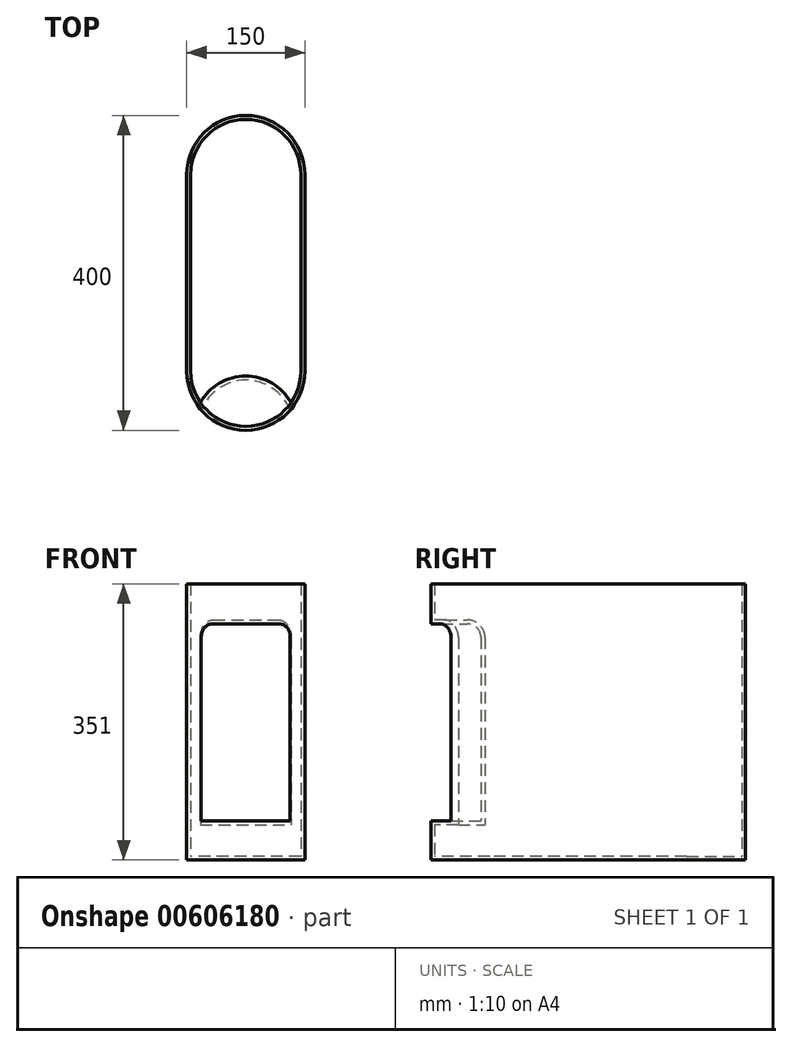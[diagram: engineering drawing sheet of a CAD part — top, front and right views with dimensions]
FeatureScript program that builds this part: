
annotation { "Feature Type Name" : "Feature", "Feature Type Description" : "" }
export const myFeature = defineFeature(function(context is Context, id is Id, definition is map)
    precondition{}
    {
        {
            var Q0;
            Q0=qCreatedBy(makeId("Top.planeOp"),FACE);
            var sketch = newSketch(context, id + "F0", { "sketchPlane" : qUnion([Q0])});
            skLineSegment(sketch, "E0", {"start": v(0, 200) * mm, "end": v(0, -200) * mm, "construction": true});
            skArc(sketch, "E1", {"start": v(75, 125) * mm, "mid": v(0, 200) * mm, "end": v(-75, 125) * mm});
            skArc(sketch, "E2", {"start": v(-75, -125) * mm, "mid": v(0, -200) * mm, "end": v(75, -125) * mm});
            skLineSegment(sketch, "E3", {"start": v(-75, 125) * mm, "end": v(-75, -125) * mm});
            skLineSegment(sketch, "E4", {"start": v(75, 125) * mm, "end": v(75, -125) * mm});
            skSolve(sketch);
        }
        {
            var Q0;
            Q0 = qSketchRegion(id + "F0", true);
            extrude(context, id + "F1", {"entities" : qUnion([Q0]), "depth" : 350 * mm, "offsetDistance" : 25 * mm});
        }
        {
            var Q0;
            Q0=qCreatedBy(makeId("Right.planeOp"),FACE);
            var sketch = newSketch(context, id + "F2", { "sketchPlane" : qUnion([Q0])});
            skLineSegment(sketch, "E5.bottom", {"start": v(-258.2, 300) * mm, "end": v(-197.2, 300) * mm});
            skLineSegment(sketch, "E5.top", {"start": v(-258.2, 50) * mm, "end": v(-197.2, 50) * mm});
            skLineSegment(sketch, "E5.left", {"start": v(-258.2, 300) * mm, "end": v(-258.2, 50) * mm});
            skLineSegment(sketch, "E5.right", {"start": v(-197.2, 300) * mm, "end": v(-197.2, 50) * mm});
            skSolve(sketch);
        }
        {
            var Q0;
            Q0=makeQuery(id+"F1.opExtrude","CAP_FACE",FACE,{"disambiguationData":[OSD([sQuery(id+"F0.wireOp",EDGE,"E1"),sQuery(id+"F0.wireOp",EDGE,"E2"),sQuery(id+"F0.wireOp",EDGE,"E3"),sQuery(id+"F0.wireOp",EDGE,"E4")])],"isStart":false});
            var sketch = newSketch(context, id + "F3", { "sketchPlane" : qUnion([Q0])});
            skSolve(sketch);
        }
        {
            var Q0;
            Q0=makeQuery(id+"F3.imprint","IMPRINT",FACE,{"disambiguationData":[TD([[makeQuery(id+"F3.imprint","IMPRINT",EDGE,{"derivedFrom":makeQuery(id+"F1.opExtrude","CAP_EDGE",EDGE,{"disambiguationData":[OSD([sQuery(id+"F0.wireOp",EDGE,"E1")])],"isStart":false})}),1.0]])]});
            extrude(context, id + "F4", {"entities" : qUnion([Q0]), "operationType" : NewBodyOperationType.ADD, "depth" : 1 * mm, "offsetDistance" : 25 * mm});
        }
        {
            var Q0;
            Q0=makeQuery(id+"F2.imprint","IMPRINT",FACE,{"disambiguationData":[TD([[makeQuery(id+"F2.imprint","IMPRINT",EDGE,{"derivedFrom":sQuery(id+"F2.wireOp",EDGE,"E5.bottom")}),-1.0]])]});
            var Q1;
            Q1=sQuery(id+"F2.wireOp",EDGE,"E5.right");
            revolve(context, id + "F5", {"operationType" : NewBodyOperationType.REMOVE, "entities" : qUnion([Q0]), "axis" : qUnion([Q1]), "revolveType" : RevolveType.FULL, "oppositeDirection" : true});
        }
        {
            var Q0;
            Q0=makeQuery(id+"F5.boolean.opBoolean","COPY",EDGE,{"derivedFrom":makeQuery(id+"F5.opRevolve","SWEPT_EDGE",EDGE,{"disambiguationData":[OSD([sQuery(id+"F2.wireOp",EDGE,"E5.bottom"),sQuery(id+"F2.wireOp",EDGE,"E5.left")])]})});
            fillet(context, id + "F6", {"entities" : qUnion([Q0]), "radius" : 17.09 * mm, "tangentPropagation" : true, "allowEdgeOverflow" : false});
        }
        {
            var Q0;
            Q0=makeQuery(id+"F4.opExtrude","CAP_FACE",FACE,{"disambiguationData":[OSD([sQuery(id+"F0.wireOp",EDGE,"E1"),sQuery(id+"F0.wireOp",EDGE,"E2"),sQuery(id+"F0.wireOp",EDGE,"E3"),sQuery(id+"F0.wireOp",EDGE,"E4")])],"isStart":false});
            shell(context, id + "F7", {"entities" : qUnion([Q0]), "thickness" : 5 * mm});
        }
    });
